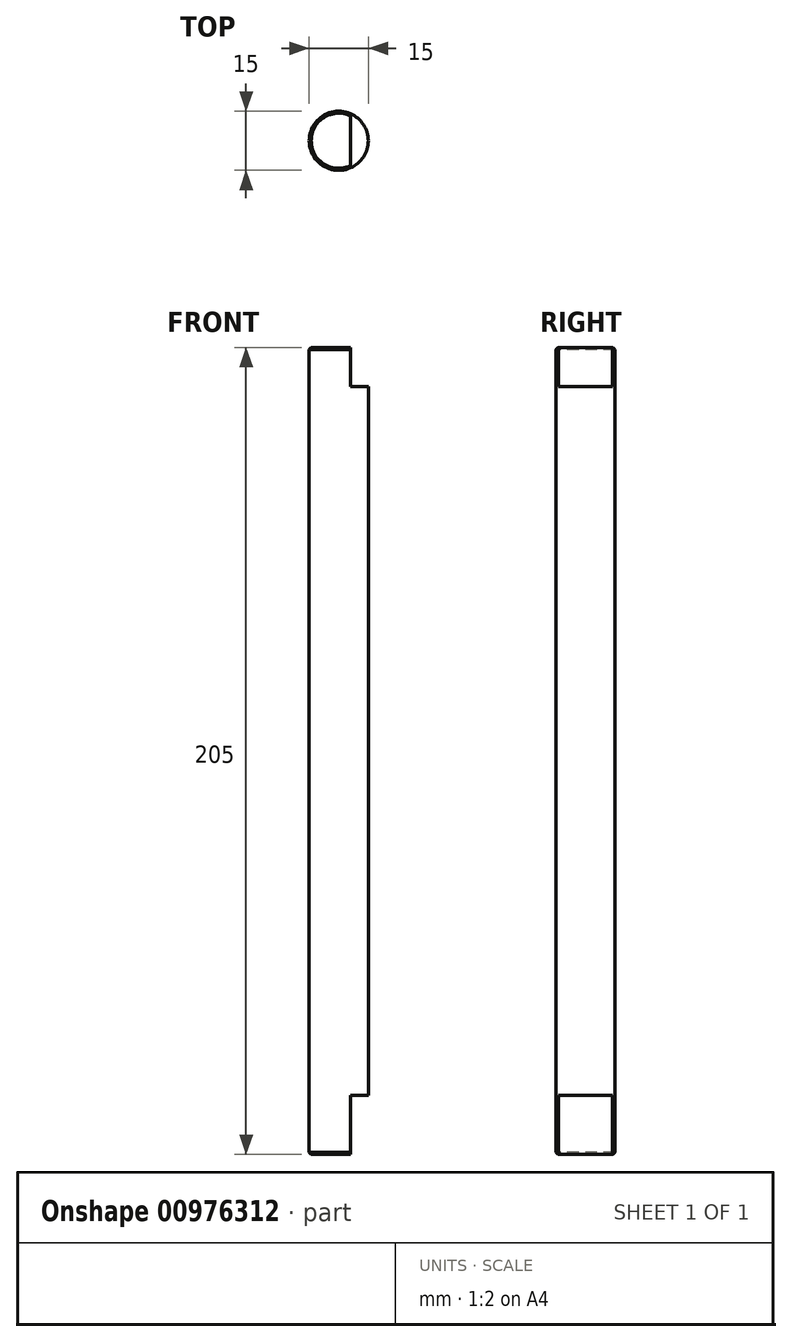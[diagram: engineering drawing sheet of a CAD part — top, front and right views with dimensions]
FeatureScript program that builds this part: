
annotation { "Feature Type Name" : "Feature", "Feature Type Description" : "" }
export const myFeature = defineFeature(function(context is Context, id is Id, definition is map)
    precondition{}
    {
        {
            var Q0;
            Q0=qCreatedBy(makeId("Top.planeOp"),FACE);
            var sketch = newSketch(context, id + "F0", { "sketchPlane" : qUnion([Q0])});
            skCircle(sketch, "E0", {"center": v(-625.09, 134.08) * mm, "radius": 7.5 * mm});
            skSolve(sketch);
        }
        {
            var Q0;
            Q0=makeQuery(id+"F0.imprint","IMPRINT",FACE,{"disambiguationData":[TD([[makeQuery(id+"F0.imprint","IMPRINT",EDGE,{"derivedFrom":sQuery(id+"F0.wireOp",EDGE,"E0")}),1.0]])]});
            extrude(context, id + "F1", {"entities" : qUnion([Q0]), "depth" : 205 * mm, "offsetDistance" : 25 * mm});
        }
        {
            var Q0;
            Q0=makeQuery(id+"F1.opExtrude","CAP_FACE",FACE,{"disambiguationData":[OSD([sQuery(id+"F0.wireOp",EDGE,"E0")])],"isStart":false});
            var sketch = newSketch(context, id + "F2", { "sketchPlane" : qUnion([Q0])});
            skLineSegment(sketch, "E1", {"start": v(-622.09, 140.96) * mm, "end": v(-622.09, 127.2) * mm});
            skSolve(sketch);
        }
        {
            var Q0;
            Q0=makeQuery(id+"F1.opExtrude","CAP_FACE",FACE,{"disambiguationData":[OSD([sQuery(id+"F0.wireOp",EDGE,"E0")])],"isStart":true});
            var sketch = newSketch(context, id + "F3", { "sketchPlane" : qUnion([Q0])});
            skLineSegment(sketch, "E2", {"start": v(-622.09, -127.2) * mm, "end": v(-622.09, -140.96) * mm});
            skSolve(sketch);
        }
        {
            var Q0;
            {var subQ0=sQuery(id+"F2.wireOp",EDGE,"E1");Q0=makeQuery(id+"F2.imprint","IMPRINT",FACE,{"disambiguationData":[TD([[makeQuery(id+"F2.imprint","IMPRINT",EDGE,{"derivedFrom":subQ0}),1.0]])]});}
            extrude(context, id + "F4", {"entities" : qUnion([Q0]), "operationType" : NewBodyOperationType.REMOVE, "oppositeDirection" : true, "depth" : 10 * mm, "offsetDistance" : 25 * mm});
        }
        {
            var Q0;
            {var subQ0=sQuery(id+"F3.wireOp",EDGE,"E2");Q0=makeQuery(id+"F3.imprint","IMPRINT",FACE,{"disambiguationData":[TD([[makeQuery(id+"F3.imprint","IMPRINT",EDGE,{"derivedFrom":subQ0}),1.0]])]});}
            extrude(context, id + "F5", {"entities" : qUnion([Q0]), "operationType" : NewBodyOperationType.REMOVE, "oppositeDirection" : true, "depth" : 15 * mm, "offsetDistance" : 25 * mm});
        }
        {
            var Q0;
            Q0=makeQuery(id+"F1.opExtrude","CAP_EDGE",EDGE,{"disambiguationData":[OSD([sQuery(id+"F0.wireOp",EDGE,"E0")])],"isStart":true});
            var Q1;
            Q1=makeQuery(id+"F1.opExtrude","CAP_EDGE",EDGE,{"disambiguationData":[OSD([sQuery(id+"F0.wireOp",EDGE,"E0")])],"isStart":false});
            chamfer(context, id + "F6", {"entities" : qUnion([Q0, Q1]), "width" : 0.5 * mm, "tangentPropagation" : true});
        }
    });
